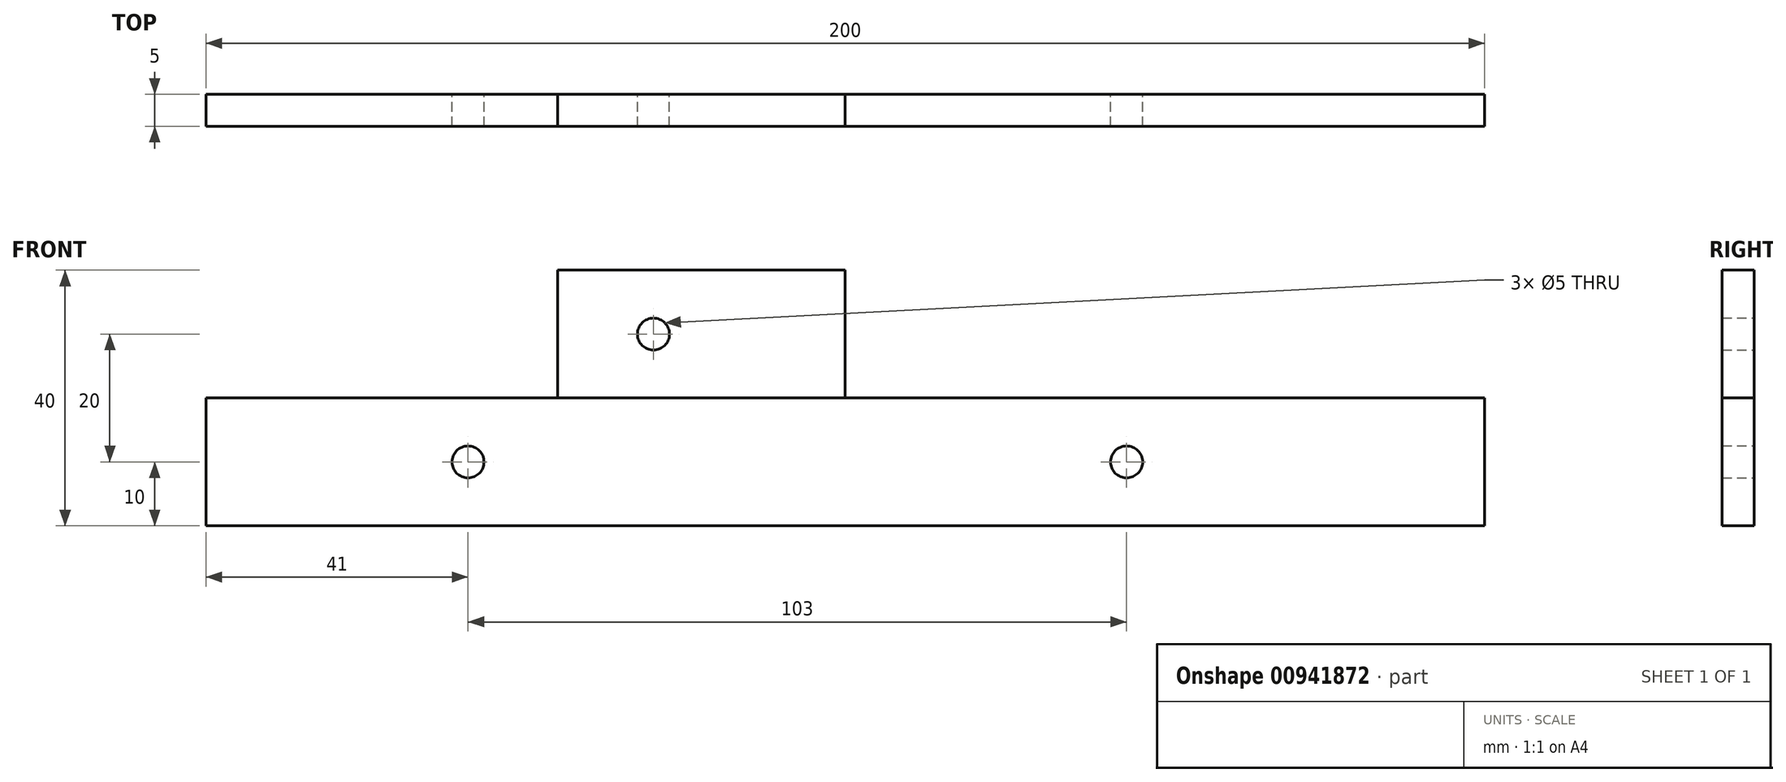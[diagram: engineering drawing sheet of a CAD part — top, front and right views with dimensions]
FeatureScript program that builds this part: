
annotation { "Feature Type Name" : "Feature", "Feature Type Description" : "" }
export const myFeature = defineFeature(function(context is Context, id is Id, definition is map)
    precondition{}
    {
        {
            var Q0;
            Q0=qCreatedBy(makeId("Front.planeOp"),FACE);
            var sketch = newSketch(context, id + "F0", { "sketchPlane" : qUnion([Q0])});
            skLineSegment(sketch, "E0", {"start": v(0, 0) * mm, "end": v(-100, 0) * mm});
            skLineSegment(sketch, "E1", {"start": v(-100, 0) * mm, "end": v(-100, -20) * mm});
            skLineSegment(sketch, "E2.MirrorCS", {"start": v(0, 0) * mm, "end": v(100, 0) * mm});
            skLineSegment(sketch, "E3.MirrorCS", {"start": v(100, 0) * mm, "end": v(100, -20) * mm});
            skLineSegment(sketch, "E4", {"start": v(-100, -20) * mm, "end": v(100, -20) * mm});
            skCircle(sketch, "E5", {"center": v(-59, -10) * mm, "radius": 2.5 * mm});
            skCircle(sketch, "E6", {"center": v(44, -10) * mm, "radius": 2.5 * mm});
            skSolve(sketch);
        }
        {
            var Q0;
            {var subQ1=sQuery(id+"F0.wireOp",EDGE,"E0");Q0=makeQuery(id+"F0.imprint","IMPRINT",FACE,{"disambiguationData":[TD([[makeQuery(id+"F0.imprint","IMPRINT",EDGE,{"derivedFrom":subQ1}),1.0]])]});}
            extrude(context, id + "F1", {"entities" : qUnion([Q0]), "depth" : 5 * mm, "offsetDistance" : 25 * mm});
        }
        {
            var Q0;
            Q0=qCreatedBy(makeId("Front.planeOp"),FACE);
            var sketch = newSketch(context, id + "F2", { "sketchPlane" : qUnion([Q0])});
            skLineSegment(sketch, "E7.bottom", {"start": v(0, 0) * mm, "end": v(-45, 0) * mm});
            skLineSegment(sketch, "E7.top", {"start": v(0, 20) * mm, "end": v(-45, 20) * mm});
            skLineSegment(sketch, "E7.left", {"start": v(0, 0) * mm, "end": v(0, 20) * mm});
            skLineSegment(sketch, "E7.right", {"start": v(-45, 0) * mm, "end": v(-45, 20) * mm});
            skLineSegment(sketch, "E8", {"start": v(-45, 10) * mm, "end": v(-30, 10) * mm});
            skCircle(sketch, "E9", {"center": v(-30, 10) * mm, "radius": 2.5 * mm});
            skSolve(sketch);
        }
        {
            var Q0;
            {var subQ1=sQuery(id+"F2.wireOp",EDGE,"E7.bottom");Q0=makeQuery(id+"F2.imprint","IMPRINT",FACE,{"disambiguationData":[TD([[makeQuery(id+"F2.imprint","IMPRINT",EDGE,{"derivedFrom":subQ1}),-1.0]])]});}
            extrude(context, id + "F3", {"entities" : qUnion([Q0]), "depth" : 5 * mm, "offsetDistance" : 25 * mm});
        }
    });
